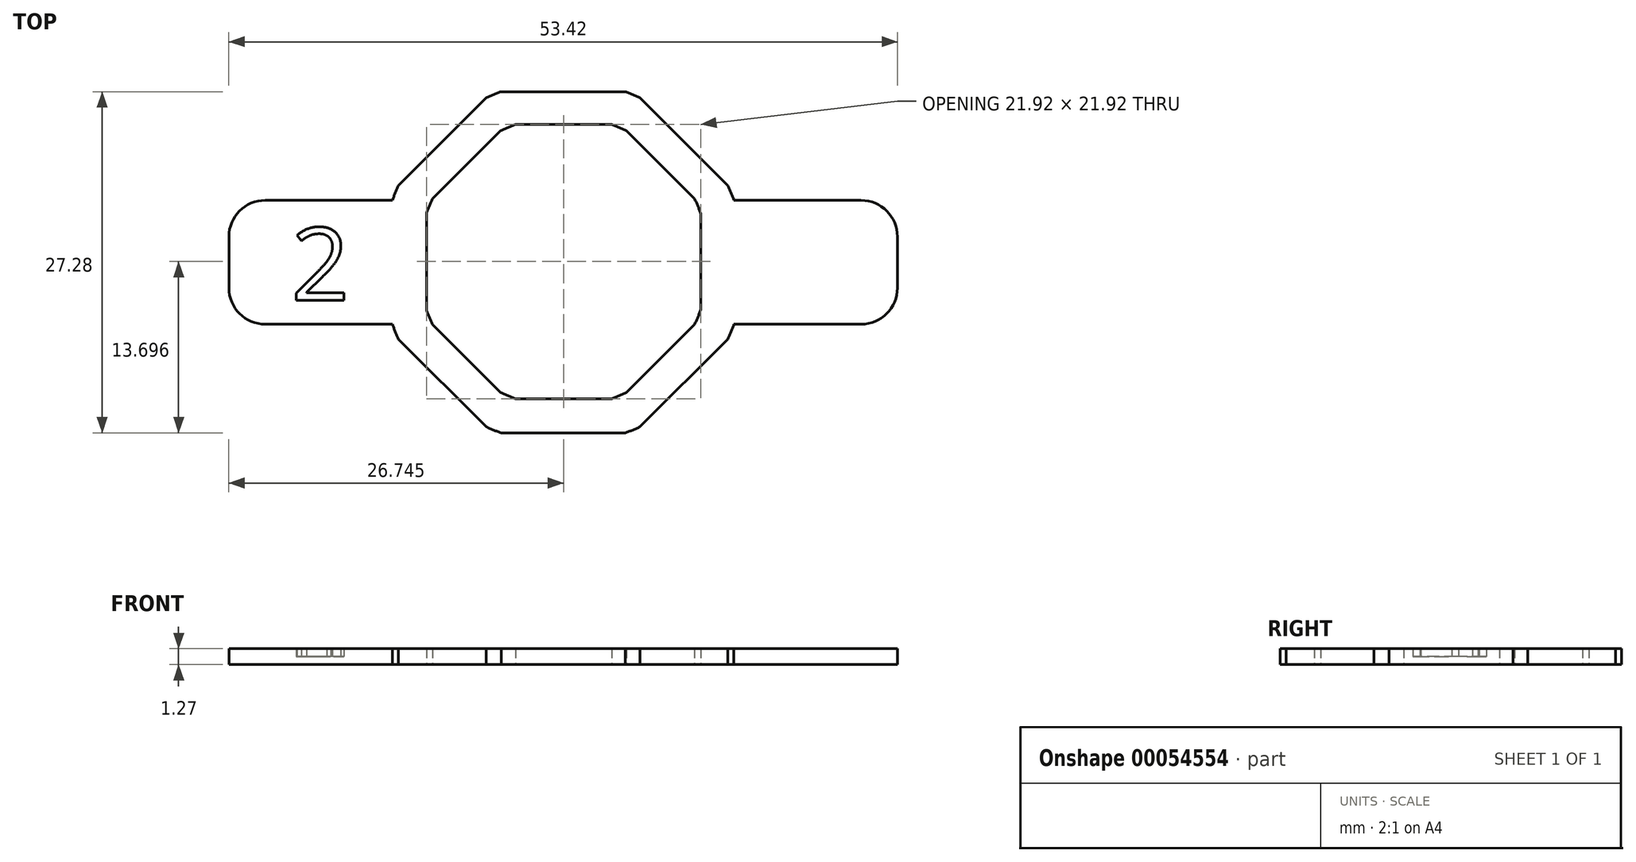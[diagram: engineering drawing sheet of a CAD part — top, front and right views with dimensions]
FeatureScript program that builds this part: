
annotation { "Feature Type Name" : "Feature", "Feature Type Description" : "" }
export const myFeature = defineFeature(function(context is Context, id is Id, definition is map)
    precondition{}
    {
        {
            var Q0;
            Q0=qCreatedBy(makeId("Top.planeOp"),FACE);
            var sketch = newSketch(context, id + "F0", { "sketchPlane" : qUnion([Q0])});
            skArc(sketch, "E0", {"start": v(-13.15, 6.15) * mm, "mid": v(-13.4, 5.55) * mm, "end": v(-13.64, 4.95) * mm});
            skLineSegment(sketch, "E1", {"start": v(-4.95, 13.64) * mm, "end": v(4.95, 13.64) * mm});
            skPoint(sketch, "E2.end.orphan", {"position": v(0, 13.64) * mm});
            skPoint(sketch, "E2.start.orphan", {"position": v(0, 14.51) * mm});
            skLineSegment(sketch, "E3.1.0", {"start": v(-13.15, 6.15) * mm, "end": v(-6.15, 13.15) * mm});
            skLineSegment(sketch, "E3.2.0", {"start": v(-13.64, -4.95) * mm, "end": v(-13.64, 4.95) * mm});
            skLineSegment(sketch, "E3.3.0", {"start": v(-6.15, -13.15) * mm, "end": v(-13.15, -6.15) * mm});
            skLineSegment(sketch, "E3.4.0", {"start": v(4.95, -13.64) * mm, "end": v(-4.95, -13.64) * mm});
            skLineSegment(sketch, "E3.5.0", {"start": v(13.15, -6.15) * mm, "end": v(6.15, -13.15) * mm});
            skLineSegment(sketch, "E3.6.0", {"start": v(13.64, 4.95) * mm, "end": v(13.64, -4.95) * mm});
            skLineSegment(sketch, "E3.7.0", {"start": v(6.15, 13.15) * mm, "end": v(13.15, 6.15) * mm});
            skArc(sketch, "E4.trimOffspring", {"start": v(-4.95, 13.64) * mm, "mid": v(-5.55, 13.4) * mm, "end": v(-6.15, 13.15) * mm});
            skArc(sketch, "E5.trimOffspring", {"start": v(6.15, 13.15) * mm, "mid": v(5.55, 13.4) * mm, "end": v(4.95, 13.64) * mm});
            skArc(sketch, "E6.trimOffspring", {"start": v(13.64, 4.95) * mm, "mid": v(13.4, 5.55) * mm, "end": v(13.15, 6.15) * mm});
            skArc(sketch, "E7.trimOffspring", {"start": v(13.15, -6.15) * mm, "mid": v(13.4, -5.55) * mm, "end": v(13.64, -4.95) * mm});
            skArc(sketch, "E8.trimOffspring", {"start": v(-6.15, -13.15) * mm, "mid": v(-5.55, -13.4) * mm, "end": v(-4.95, -13.64) * mm});
            skArc(sketch, "E9.trimOffspring", {"start": v(-13.64, -4.95) * mm, "mid": v(-13.4, -5.55) * mm, "end": v(-13.15, -6.15) * mm});
            skArc(sketch, "E10.trimOffspring", {"start": v(4.95, -13.64) * mm, "mid": v(5.55, -13.4) * mm, "end": v(6.15, -13.15) * mm});
            skLineSegment(sketch, "E11.6.0", {"start": v(11, 3.9) * mm, "end": v(11, -3.78) * mm});
            skLineSegment(sketch, "E11.4.0", {"start": v(3.87, -10.9) * mm, "end": v(-3.8, -10.9) * mm});
            skLineSegment(sketch, "E11.3.0", {"start": v(-5, -10.4) * mm, "end": v(-10.43, -4.98) * mm});
            skLineSegment(sketch, "E11.7.0", {"start": v(5.07, 10.52) * mm, "end": v(10.5, 5.09) * mm});
            skLineSegment(sketch, "E11.5.0", {"start": v(10.5, -4.98) * mm, "end": v(5.07, -10.4) * mm});
            skPoint(sketch, "E12.start.orphan", {"position": v(0.03, 11.67) * mm});
            skLineSegment(sketch, "E11.2.0", {"start": v(-10.92, -3.78) * mm, "end": v(-10.92, 3.9) * mm});
            skLineSegment(sketch, "E11.1.0", {"start": v(-10.43, 5.09) * mm, "end": v(-5, 10.52) * mm});
            skLineSegment(sketch, "E13", {"start": v(-3.8, 11.01) * mm, "end": v(3.87, 11.01) * mm});
            skPoint(sketch, "E12.end.orphan", {"position": v(0.03, 11.01) * mm});
            skPoint(sketch, "E11.center", {"position": v(0.03, 0.06) * mm});
            skArc(sketch, "E14.trimOffspring", {"start": v(3.87, -10.9) * mm, "mid": v(4.48, -10.67) * mm, "end": v(5.07, -10.4) * mm});
            skArc(sketch, "E15.trimOffspring", {"start": v(5.07, 10.52) * mm, "mid": v(4.48, 10.78) * mm, "end": v(3.87, 11.01) * mm});
            skArc(sketch, "E16.trimOffspring", {"start": v(-3.8, 11.01) * mm, "mid": v(-4.4, 10.78) * mm, "end": v(-5, 10.52) * mm});
            skArc(sketch, "E17", {"start": v(-10.43, 5.09) * mm, "mid": v(-10.7, 4.5) * mm, "end": v(-10.92, 3.9) * mm});
            skArc(sketch, "E18.trimOffspring", {"start": v(11, 3.9) * mm, "mid": v(10.76, 4.5) * mm, "end": v(10.5, 5.09) * mm});
            skArc(sketch, "E19.trimOffspring", {"start": v(-10.92, -3.78) * mm, "mid": v(-10.7, -4.39) * mm, "end": v(-10.43, -4.98) * mm});
            skArc(sketch, "E20.trimOffspring", {"start": v(-5, -10.4) * mm, "mid": v(-4.4, -10.67) * mm, "end": v(-3.8, -10.9) * mm});
            skArc(sketch, "E21.trimOffspring", {"start": v(10.5, -4.98) * mm, "mid": v(10.76, -4.39) * mm, "end": v(11, -3.78) * mm});
            skLineSegment(sketch, "E22.bottom", {"start": v(-13.64, 4.95) * mm, "end": v(-23.8, 4.95) * mm});
            skLineSegment(sketch, "E22.top", {"start": v(-13.64, -4.95) * mm, "end": v(-23.8, -4.95) * mm});
            skLineSegment(sketch, "E22.right", {"start": v(-26.7, 2.05) * mm, "end": v(-26.7, -2.05) * mm});
            skLineSegment(sketch, "E23.bottom", {"start": v(13.64, 4.95) * mm, "end": v(23.8, 4.95) * mm});
            skLineSegment(sketch, "E23.top", {"start": v(13.64, -4.95) * mm, "end": v(23.8, -4.95) * mm});
            skLineSegment(sketch, "E23.right", {"start": v(26.7, 2.05) * mm, "end": v(26.7, -2.05) * mm});
            skPoint(sketch, "E24.visualSharp", {"position": v(-26.7, 4.95) * mm});
            skArc(sketch, "E24.filletArc", {"start": v(-23.8, 4.95) * mm, "mid": v(-25.86, 4.1) * mm, "end": v(-26.7, 2.05) * mm});
            skPoint(sketch, "E25.visualSharp", {"position": v(-26.7, -4.95) * mm});
            skArc(sketch, "E25.filletArc", {"start": v(-26.7, -2.05) * mm, "mid": v(-25.86, -4.1) * mm, "end": v(-23.8, -4.95) * mm});
            skPoint(sketch, "E26.visualSharp", {"position": v(26.7, 4.95) * mm});
            skArc(sketch, "E26.filletArc", {"start": v(26.7, 2.05) * mm, "mid": v(25.86, 4.1) * mm, "end": v(23.8, 4.95) * mm});
            skPoint(sketch, "E27.visualSharp", {"position": v(26.7, -4.95) * mm});
            skArc(sketch, "E27.filletArc", {"start": v(23.8, -4.95) * mm, "mid": v(25.86, -4.1) * mm, "end": v(26.7, -2.05) * mm});
            skText(sketch, "E28", { "text": "2", "fontName": "OpenSans-Regular.ttf"});
            const initialGuessF0  = {"E28": [-0.02172, -0.00304, 1, 0, 0.00585]};
            skSetInitialGuess(sketch, initialGuessF0);
            skSolve(sketch);
        }
        {
            var Q0;
            Q0=makeQuery(id+"F0.imprint","IMPRINT",FACE,{"disambiguationData":[TD([[makeQuery(id+"F0.imprint","IMPRINT",EDGE,{"derivedFrom":sQuery(id+"F0.wireOp",EDGE,"E0")}),1.0]])]});
            extrude(context, id + "F1", {"entities" : qUnion([Q0]), "depth" : 1.27 * mm});
        }
        {
            var Q0;
            Q0=makeQuery(id+"F0.imprint","IMPRINT",FACE,{"disambiguationData":[TD([[makeQuery(id+"F0.imprint","IMPRINT",EDGE,{"derivedFrom":sQuery(id+"F0.wireOp",EDGE,"E3.2.0")}),1.0]])]});
            var Q1;
            Q1=makeQuery(id+"F0.imprint","IMPRINT",FACE,{"disambiguationData":[TD([[makeQuery(id+"F0.imprint","IMPRINT",EDGE,{"derivedFrom":sQuery(id+"F0.wireOp",EDGE,"E3.6.0")}),1.0]])]});
            extrude(context, id + "F2", {"entities" : qUnion([Q0, Q1]), "operationType" : NewBodyOperationType.ADD, "depth" : 1.27 * mm});
        }
        {
            var Q0;
            Q0=makeQuery(id+"F0.imprint","IMPRINT",FACE,{"disambiguationData":[TD([[makeQuery(id+"F0.imprint","IMPRINT",EDGE,{"derivedFrom":sQuery(id+"F0.wireOp",EDGE,"E28.sketch_text.stroke-0")}),-1.0]])]});
            extrude(context, id + "F3", {"entities" : qUnion([Q0]), "operationType" : NewBodyOperationType.ADD, "depth" : 0.64 * mm});
        }
    });
